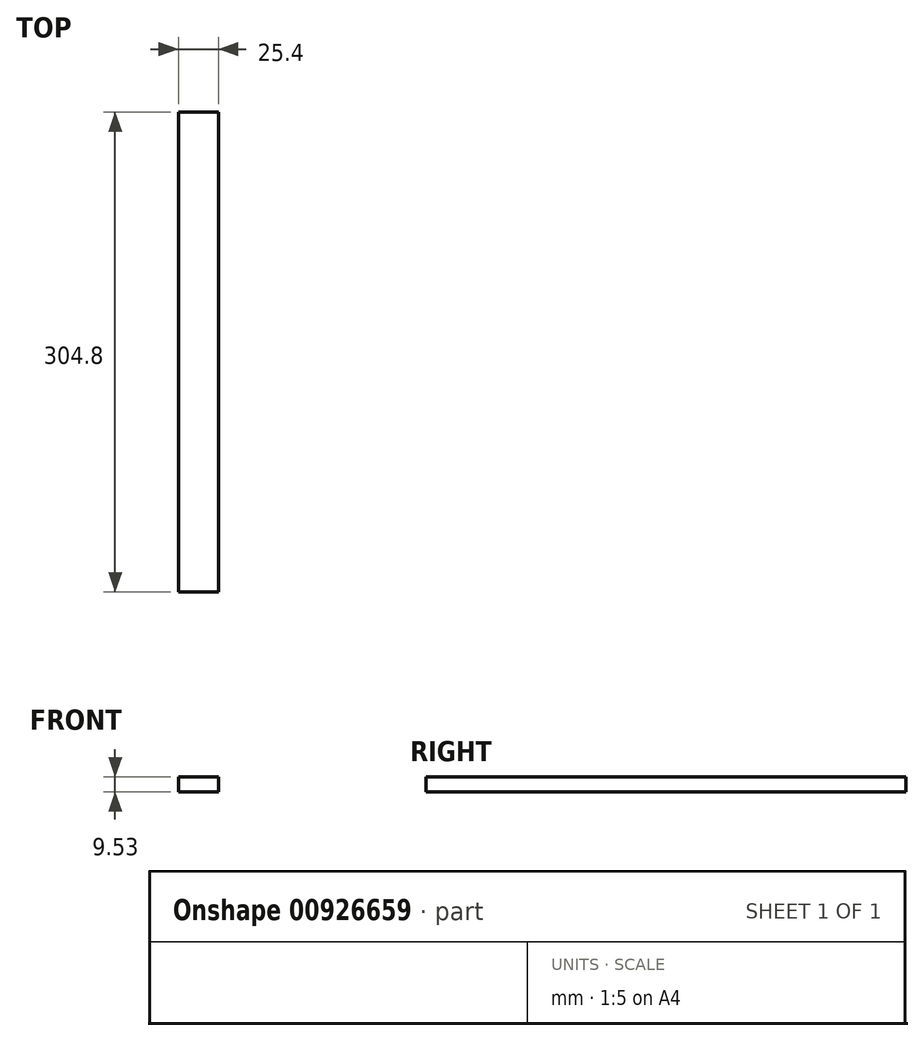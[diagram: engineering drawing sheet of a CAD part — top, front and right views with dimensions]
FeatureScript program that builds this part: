
annotation { "Feature Type Name" : "Feature", "Feature Type Description" : "" }
export const myFeature = defineFeature(function(context is Context, id is Id, definition is map)
    precondition{}
    {
        {
            var Q0;
            Q0=qCreatedBy(makeId("Top.planeOp"),FACE);
            var sketch = newSketch(context, id + "F0", { "sketchPlane" : qUnion([Q0])});
            skLineSegment(sketch, "E0.bottom", {"start": v(-27.21, 150.93) * mm, "end": v(-1.81, 150.93) * mm});
            skLineSegment(sketch, "E0.top", {"start": v(-27.21, -153.87) * mm, "end": v(-1.81, -153.87) * mm});
            skLineSegment(sketch, "E0.left", {"start": v(-27.21, 150.93) * mm, "end": v(-27.21, -153.87) * mm});
            skLineSegment(sketch, "E0.right", {"start": v(-1.81, 150.93) * mm, "end": v(-1.81, -153.87) * mm});
            skSolve(sketch);
        }
        {
            var Q0;
            Q0 = qSketchRegion(id + "F0", true);
            extrude(context, id + "F1", {"entities" : qUnion([Q0]), "depth" : 9.52 * mm, "offsetDistance" : 25.4 * mm});
        }
    });
